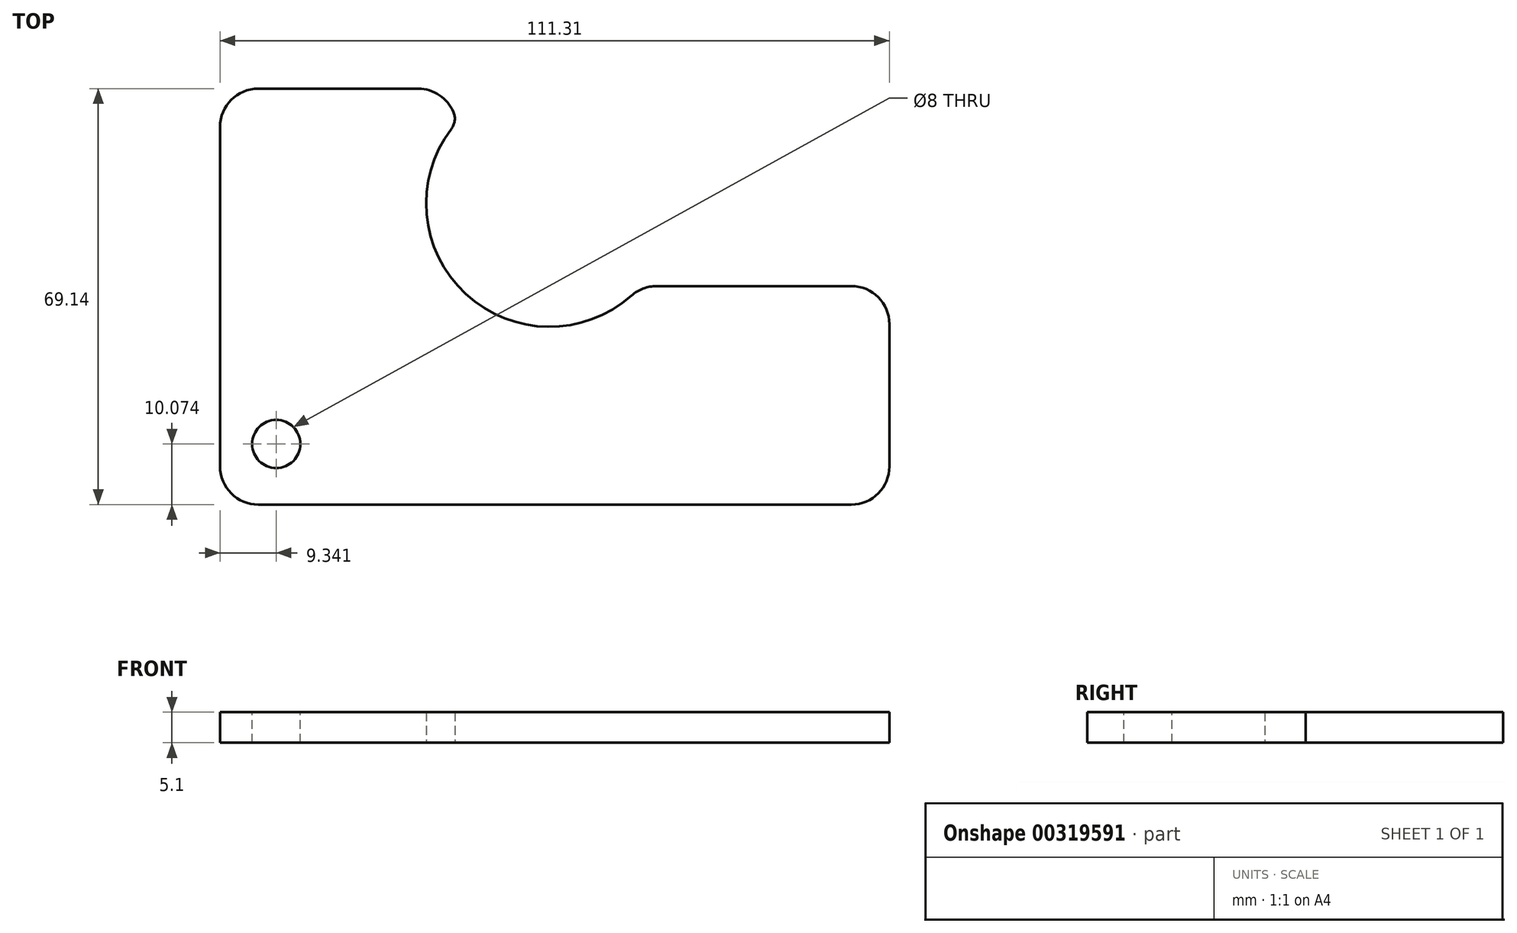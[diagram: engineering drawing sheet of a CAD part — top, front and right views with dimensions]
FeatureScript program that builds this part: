
annotation { "Feature Type Name" : "Feature", "Feature Type Description" : "" }
export const myFeature = defineFeature(function(context is Context, id is Id, definition is map)
    precondition{}
    {
        {
            var Q0;
            Q0=qCreatedBy(makeId("Top.planeOp"),FACE);
            var sketch = newSketch(context, id + "F0", { "sketchPlane" : qUnion([Q0])});
            skLineSegment(sketch, "E0.bottom", {"start": v(-61.12, 26.33) * mm, "end": v(-34.5, 26.33) * mm});
            skLineSegment(sketch, "E0.top", {"start": v(-61.12, -42.8) * mm, "end": v(-28.16, -42.8) * mm});
            skLineSegment(sketch, "E0.left", {"start": v(-67.47, 19.98) * mm, "end": v(-67.47, -36.46) * mm});
            skLineSegment(sketch, "E1.bottom", {"start": v(37.5, -42.8) * mm, "end": v(-28.16, -42.8) * mm});
            skLineSegment(sketch, "E1.top", {"start": v(37.5, -6.48) * mm, "end": v(5.15, -6.48) * mm});
            skLineSegment(sketch, "E1.left", {"start": v(43.84, -36.46) * mm, "end": v(43.84, -12.83) * mm});
            skLineSegment(sketch, "E2", {"start": v(-28.16, -6.48) * mm, "end": v(-28.16, -6.48) * mm});
            skPoint(sketch, "E3.visualSharp", {"position": v(43.84, -6.48) * mm});
            skArc(sketch, "E3.filletArc", {"start": v(43.84, -12.83) * mm, "mid": v(41.98, -8.34) * mm, "end": v(37.5, -6.48) * mm});
            skPoint(sketch, "E4.visualSharp", {"position": v(-28.16, 26.33) * mm});
            skArc(sketch, "E4.filletArc", {"start": v(-28.65, 22.44) * mm, "mid": v(-31, 25.27) * mm, "end": v(-34.5, 26.33) * mm});
            skPoint(sketch, "E5.visualSharp", {"position": v(43.84, -42.8) * mm});
            skArc(sketch, "E5.filletArc", {"start": v(37.5, -42.8) * mm, "mid": v(41.98, -40.95) * mm, "end": v(43.84, -36.46) * mm});
            skPoint(sketch, "E6.visualSharp", {"position": v(-67.47, -42.8) * mm});
            skArc(sketch, "E6.filletArc", {"start": v(-67.47, -36.46) * mm, "mid": v(-65.61, -40.95) * mm, "end": v(-61.12, -42.8) * mm});
            skPoint(sketch, "E7.visualSharp", {"position": v(-67.47, 26.33) * mm});
            skArc(sketch, "E7.filletArc", {"start": v(-61.12, 26.33) * mm, "mid": v(-65.61, 24.47) * mm, "end": v(-67.47, 19.98) * mm});
            skArc(sketch, "E8", {"start": v(-29, 19.64) * mm, "mid": v(-26.6, -7.8) * mm, "end": v(0.93, -8.08) * mm});
            skPoint(sketch, "E9.visualSharp", {"position": v(2.54, -6.48) * mm});
            skArc(sketch, "E9.filletArc", {"start": v(5.15, -6.48) * mm, "mid": v(2.9, -6.9) * mm, "end": v(0.93, -8.08) * mm});
            skPoint(sketch, "E10.visualSharp", {"position": v(-28.2, 20.65) * mm});
            skArc(sketch, "E10.filletArc", {"start": v(-29, 19.64) * mm, "mid": v(-28.46, 21) * mm, "end": v(-28.65, 22.44) * mm});
            skSolve(sketch);
        }
        {
            var Q0;
            Q0=makeQuery(id+"F0.imprint","IMPRINT",FACE,{"disambiguationData":[TD([[makeQuery(id+"F0.imprint","IMPRINT",EDGE,{"derivedFrom":sQuery(id+"F0.wireOp",EDGE,"E0.bottom")}),-1.0]])]});
            extrude(context, id + "F1", {"entities" : qUnion([Q0]), "depth" : 5.1 * mm});
        }
        {
            var Q0;
            Q0=makeQuery(id+"F1.opExtrude","SWEPT_BODY",BODY,{"disambiguationData":[OSD([sQuery(id+"F0.wireOp",EDGE,"E0.bottom"),sQuery(id+"F0.wireOp",EDGE,"E0.top"),sQuery(id+"F0.wireOp",EDGE,"E0.left"),sQuery(id+"F0.wireOp",EDGE,"E0.right"),sQuery(id+"F0.wireOp",EDGE,"E1.bottom"),sQuery(id+"F0.wireOp",EDGE,"E1.top"),sQuery(id+"F0.wireOp",EDGE,"E1.left"),sQuery(id+"F0.wireOp",EDGE,"E2"),sQuery(id+"F0.wireOp",EDGE,"E3.filletArc"),sQuery(id+"F0.wireOp",EDGE,"E4.filletArc"),sQuery(id+"F0.wireOp",EDGE,"E2"),sQuery(id+"F0.wireOp",EDGE,"E2")])]});
            transform(context, id + "F2", {"entities" : qUnion([Q0]), "transformType" : TransformType.TRANSLATION_3D, "dx" : 20.7 * mm, "dy" : 0 * mm, "dz" : 0 * mm, "makeCopy" : false});
        }
        {
            var Q0;
            Q0=makeQuery(id+"F1.opExtrude","CAP_FACE",FACE,{"disambiguationData":[OSD([sQuery(id+"F0.wireOp",EDGE,"E0.bottom"),sQuery(id+"F0.wireOp",EDGE,"E0.top"),sQuery(id+"F0.wireOp",EDGE,"E0.left"),sQuery(id+"F0.wireOp",EDGE,"E0.right"),sQuery(id+"F0.wireOp",EDGE,"E1.bottom"),sQuery(id+"F0.wireOp",EDGE,"E1.top"),sQuery(id+"F0.wireOp",EDGE,"E1.left"),sQuery(id+"F0.wireOp",EDGE,"E3.filletArc"),sQuery(id+"F0.wireOp",EDGE,"E4.filletArc"),sQuery(id+"F0.wireOp",EDGE,"E5.filletArc"),sQuery(id+"F0.wireOp",EDGE,"E6.filletArc"),sQuery(id+"F0.wireOp",EDGE,"E7.filletArc"),sQuery(id+"F0.wireOp",EDGE,"E8"),sQuery(id+"F0.wireOp",EDGE,"5697f377-a4ee-43b8-91ef-bd139bf05c62.trimOffspring"),sQuery(id+"F0.wireOp",EDGE,"E9.filletArc"),sQuery(id+"F0.wireOp",EDGE,"E10.filletArc")])],"isStart":false});
            var sketch = newSketch(context, id + "F3", { "sketchPlane" : qUnion([Q0])});
            skCircle(sketch, "E11", {"center": v(-37.43, -32.74) * mm, "radius": 4 * mm});
            skSolve(sketch);
        }
        {
            var Q0;
            Q0=makeQuery(id+"F3.imprint","IMPRINT",FACE,{"disambiguationData":[TD([[makeQuery(id+"F3.imprint","IMPRINT",EDGE,{"derivedFrom":sQuery(id+"F3.wireOp",EDGE,"E11")}),1.0]])]});
            extrude(context, id + "F4", {"entities" : qUnion([Q0]), "operationType" : NewBodyOperationType.REMOVE, "oppositeDirection" : true, "depth" : 13.8 * mm, "offsetDistance" : 25 * mm});
        }
    });
